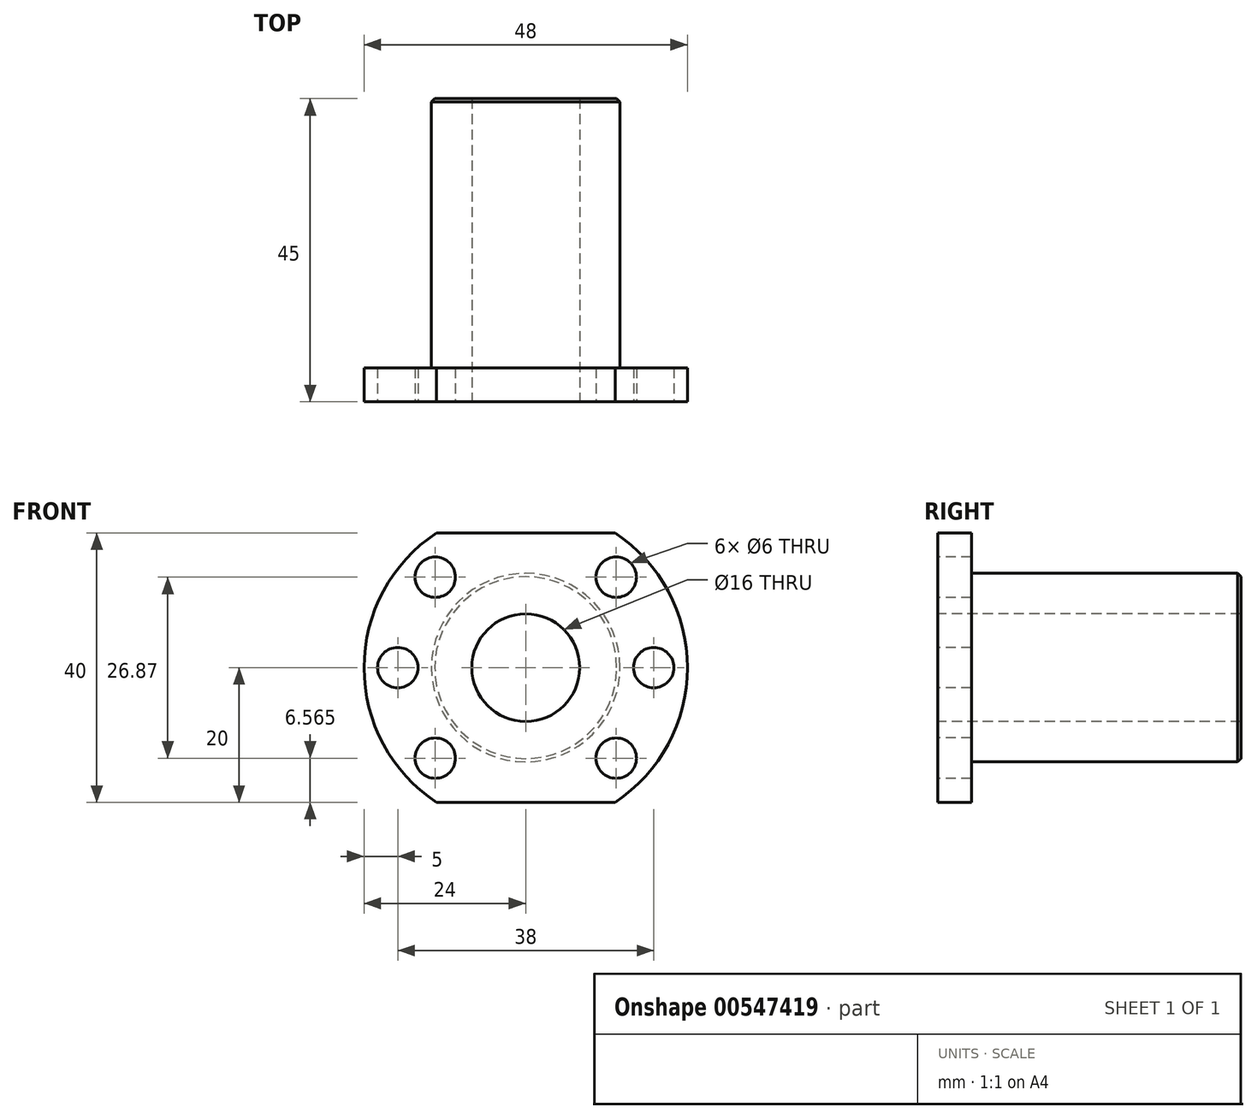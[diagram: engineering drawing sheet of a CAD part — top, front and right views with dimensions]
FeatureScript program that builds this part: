
annotation { "Feature Type Name" : "Feature", "Feature Type Description" : "" }
export const myFeature = defineFeature(function(context is Context, id is Id, definition is map)
    precondition{}
    {
        {
            var Q0;
            Q0=qCreatedBy(makeId("Right.planeOp"),FACE);
            var sketch = newSketch(context, id + "F0", { "sketchPlane" : qUnion([Q0])});
            skLineSegment(sketch, "E0.bottom", {"start": v(0, 0) * mm, "end": v(40, 0) * mm});
            skLineSegment(sketch, "E0.top", {"start": v(0, 14) * mm, "end": v(40, 14) * mm});
            skLineSegment(sketch, "E0.left", {"start": v(0, 0) * mm, "end": v(0, 14) * mm});
            skLineSegment(sketch, "E0.right", {"start": v(40, 0) * mm, "end": v(40, 14) * mm});
            skLineSegment(sketch, "E1.bottom", {"start": v(0, 0) * mm, "end": v(-5, 0) * mm});
            skLineSegment(sketch, "E1.top", {"start": v(0, 24) * mm, "end": v(-5, 24) * mm});
            skLineSegment(sketch, "E1.left", {"start": v(0, 0) * mm, "end": v(0, 24) * mm});
            skLineSegment(sketch, "E1.right", {"start": v(-5, 0) * mm, "end": v(-5, 24) * mm});
            skSolve(sketch);
        }
        {
            var Q0;
            Q0 = qSketchRegion(id + "F0", true);
            var Q1;
            Q1=sQuery(id+"F0.wireOp",EDGE,"E0.bottom");
            revolve(context, id + "F1", {"entities" : qUnion([Q0]), "axis" : qUnion([Q1]), "revolveType" : RevolveType.FULL});
        }
        {
            var Q0;
            Q0=makeQuery(id+"F1.opRevolve","SWEPT_FACE",FACE,{"disambiguationData":[OSD([sQuery(id+"F0.wireOp",EDGE,"E1.right")])]});
            var sketch = newSketch(context, id + "F2", { "sketchPlane" : qUnion([Q0])});
            skLineSegment(sketch, "E2.bottom", {"start": v(-13.27, 20) * mm, "end": v(13.27, 20) * mm});
            skLineSegment(sketch, "E2.top", {"start": v(-13.27, 27.6) * mm, "end": v(13.27, 27.6) * mm});
            skLineSegment(sketch, "E2.left", {"start": v(-13.27, 20) * mm, "end": v(-13.27, 27.6) * mm});
            skLineSegment(sketch, "E2.right", {"start": v(13.27, 20) * mm, "end": v(13.27, 27.6) * mm});
            skLineSegment(sketch, "E3.bottom", {"start": v(-13.27, -20) * mm, "end": v(13.27, -20) * mm});
            skLineSegment(sketch, "E3.top", {"start": v(-13.27, -29.78) * mm, "end": v(13.27, -29.78) * mm});
            skLineSegment(sketch, "E3.left", {"start": v(-13.27, -20) * mm, "end": v(-13.27, -29.78) * mm});
            skLineSegment(sketch, "E3.right", {"start": v(13.27, -20) * mm, "end": v(13.27, -29.78) * mm});
            skSolve(sketch);
        }
        {
            var Q0;
            Q0 = qSketchRegion(id + "F2", true);
            extrude(context, id + "F3", {"entities" : qUnion([Q0]), "operationType" : NewBodyOperationType.REMOVE, "oppositeDirection" : true, "depth" : 5 * mm, "offsetDistance" : 25 * mm});
        }
        {
            var Q0;
            Q0=makeQuery(id+"F1.opRevolve","SWEPT_FACE",FACE,{"disambiguationData":[OSD([sQuery(id+"F0.wireOp",EDGE,"E1.right")])]});
            var sketch = newSketch(context, id + "F4", { "sketchPlane" : qUnion([Q0])});
            skCircle(sketch, "E4", {"center": v(0, 0) * mm, "radius": 8 * mm});
            skSolve(sketch);
        }
        {
            var Q0;
            Q0 = qSketchRegion(id + "F4", true);
            extrude(context, id + "F5", {"entities" : qUnion([Q0]), "operationType" : NewBodyOperationType.REMOVE, "oppositeDirection" : true, "depth" : 45 * mm, "offsetDistance" : 25 * mm});
        }
        {
            var Q0;
            Q0=makeQuery(id+"F1.opRevolve","SWEPT_FACE",FACE,{"disambiguationData":[OSD([sQuery(id+"F0.wireOp",EDGE,"E1.right")])]});
            var sketch = newSketch(context, id + "F6", { "sketchPlane" : qUnion([Q0])});
            skCircle(sketch, "E5", {"center": v(-13.44, 13.44) * mm, "radius": 3 * mm});
            skCircle(sketch, "E6", {"center": v(13.44, 13.44) * mm, "radius": 3 * mm});
            skCircle(sketch, "E7", {"center": v(13.44, -13.44) * mm, "radius": 3 * mm});
            skCircle(sketch, "E8", {"center": v(-13.44, -13.44) * mm, "radius": 3 * mm});
            skCircle(sketch, "E9", {"center": v(-19, 0) * mm, "radius": 3 * mm});
            skCircle(sketch, "E10", {"center": v(19, 0) * mm, "radius": 3 * mm});
            skSolve(sketch);
        }
        {
            var Q0;
            Q0 = qSketchRegion(id + "F6", true);
            extrude(context, id + "F7", {"entities" : qUnion([Q0]), "operationType" : NewBodyOperationType.REMOVE, "oppositeDirection" : true, "depth" : 5 * mm, "offsetDistance" : 25 * mm});
        }
        {
            var Q0;
            Q0=makeQuery(id+"F1.opRevolve","SWEPT_EDGE",EDGE,{"disambiguationData":[OSD([sQuery(id+"F0.wireOp",EDGE,"E0.top"),sQuery(id+"F0.wireOp",EDGE,"E0.right")])]});
            chamfer(context, id + "F8", {"entities" : qUnion([Q0]), "width" : 0.5 * mm, "tangentPropagation" : true});
        }
    });
